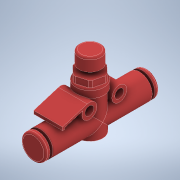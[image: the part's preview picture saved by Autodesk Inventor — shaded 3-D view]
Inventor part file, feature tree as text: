
AUTODESK INVENTOR PART (.ipt)
format: ipt  version: 2021 (Build 250183000, 183)  size: 293,376 bytes
history: native  units: mm
features: sketch x8, extrude x6, fillet x3, revolve x2, projected_geometry x2
ambient origin geometry x8: Origin, YZ Plane, XZ Plane, XY Plane, X Axis, Y Axis, Z Axis, Center Point
bodies: Solid1 (feature_tree)
feature tree (21):
  extrude  "Extrusion1"  Depth=14.0mm TaperAngle=0.0deg
  revolve  "Revolution1"  [1 undecoded]
  extrude  "Extrusion2"  TaperAngle=90.0deg  [1 undecoded]
  revolve  "Revolution2"  [1 undecoded]
  extrude  "Extrusion3"  Depth=1.0mm
  fillet  "Fillet1"  Radius=2.7mm
  fillet  "Fillet2"  Radius=1.0mm
  extrude  "Extrusion4"  Depth=4.6mm
  extrude  "Extrusion5"  Depth=4.6mm
  extrude  "Extrusion6"  Depth=3.3mm
  fillet  "Fillet3"  Radius=3.3mm
  sketch  "Sketch1"  dims[d0=9.3mm d1=14.0mm d2=0.0mm]
  sketch  "Sketch2"  dims[d3=5.1mm d4=9.3mm]
  sketch  "Sketch3"  dims[d5=36.5mm d6=90.0deg]
  sketch  "Sketch4"  dims[d7=10.3mm d8=3.2mm d9=0.0mm]
  projected_geometry  "Projected Loop1"
  projected_geometry  "Projected Loop2"
  sketch  "Sketch5"  dims[d10=2.7mm d11=1.0mm d12=2.7mm d13=1.0mm]
  sketch  "Sketch6"  dims[d14=4.6mm d15=1.6mm]
  sketch  "Sketch7"  dims[d16=4.6mm d17=1.6mm]
  sketch  "Sketch8"  dims[d18=90.0deg d19=3.3mm d20=3.3mm d21=5.5mm d22=5.5mm d23=11.8mm d24=11.8mm d25=5.5mm d26=11.0mm d27=10.6mm d28=0.0mm d29=0.7mm d30=8.9mm d31=9.75mm d32=2.35mm d33=0.0mm d34=0.7mm d35=2.9mm d36=2.0mm d37=0.0mm d38=8.0mm d39=4.6mm d40=0.0mm d41=0.7mm d42=0.8mm d43=0.8mm d44=15.4mm]
note: 3 required parameter values undecoded (feature->parameter linkage not recoverable at this tier; creation-order binding heuristic only, values carry confidence <= 0.55)